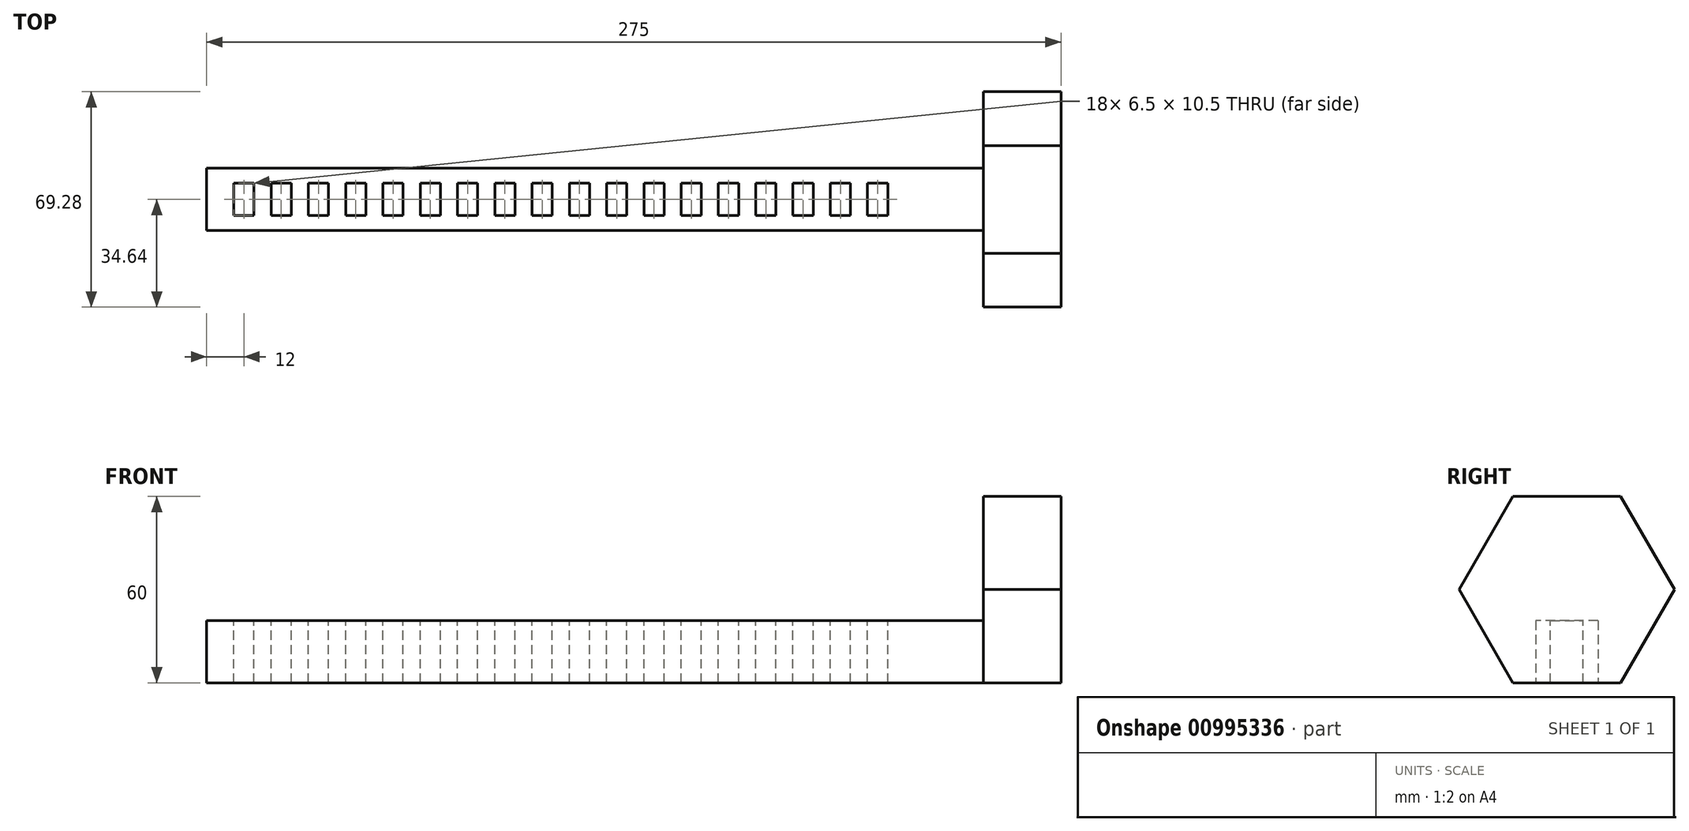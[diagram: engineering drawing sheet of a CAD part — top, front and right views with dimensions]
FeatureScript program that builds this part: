
annotation { "Feature Type Name" : "Feature", "Feature Type Description" : "" }
export const myFeature = defineFeature(function(context is Context, id is Id, definition is map)
    precondition{}
    {
        {
            var Q0;
            Q0=qCreatedBy(makeId("Right.planeOp"),FACE);
            var sketch = newSketch(context, id + "F0", { "sketchPlane" : qUnion([Q0])});
            skPoint(sketch, "E0", {"position": v(0, 0) * mm});
            skPoint(sketch, "E1", {"position": v(0, 30) * mm});
            skCircle(sketch, "E2.cCircle", {"center": v(0, 30) * mm, "radius": 30 * mm, "construction": true});
            skLineSegment(sketch, "E2.0", {"start": v(17.32, 0) * mm, "end": v(-17.32, 0) * mm});
            skLineSegment(sketch, "E2.1", {"start": v(-17.32, 0) * mm, "end": v(-34.64, 30) * mm});
            skLineSegment(sketch, "E2.2", {"start": v(-34.64, 30) * mm, "end": v(-17.32, 60) * mm});
            skLineSegment(sketch, "E2.3", {"start": v(-17.32, 60) * mm, "end": v(17.32, 60) * mm});
            skLineSegment(sketch, "E2.4", {"start": v(17.32, 60) * mm, "end": v(34.64, 30) * mm});
            skLineSegment(sketch, "E2.5", {"start": v(34.64, 30) * mm, "end": v(17.32, 0) * mm});
            skSolve(sketch);
        }
        {
            var Q0;
            Q0 = qSketchRegion(id + "F0", true);
            extrude(context, id + "F1", {"entities" : qUnion([Q0]), "depth" : 25 * mm, "offsetDistance" : 25 * mm});
        }
        {
            var Q0;
            Q0=qCreatedBy(makeId("Top.planeOp"),FACE);
            var sketch = newSketch(context, id + "F2", { "sketchPlane" : qUnion([Q0])});
            skPoint(sketch, "E3", {"position": v(0, 0) * mm});
            skPoint(sketch, "E4", {"position": v(0, 10) * mm});
            skPoint(sketch, "E5", {"position": v(0, -10) * mm});
            skLineSegment(sketch, "E6.bottom", {"start": v(0, 10) * mm, "end": v(-250, 10) * mm});
            skLineSegment(sketch, "E6.top", {"start": v(0, -10) * mm, "end": v(-250, -10) * mm});
            skLineSegment(sketch, "E6.left", {"start": v(0, 10) * mm, "end": v(0, -10) * mm});
            skLineSegment(sketch, "E6.right", {"start": v(-250, 10) * mm, "end": v(-250, -10) * mm});
            skSolve(sketch);
        }
        {
            var Q0;
            Q0 = qSketchRegion(id + "F2", true);
            extrude(context, id + "F3", {"entities" : qUnion([Q0]), "operationType" : NewBodyOperationType.ADD, "depth" : 20 * mm, "offsetDistance" : 25 * mm});
        }
        {
            var Q0;
            Q0=makeQuery(id+"F3.opExtrude","CAP_FACE",FACE,{"disambiguationData":[OSD([sQuery(id+"F2.wireOp",EDGE,"E6.bottom"),sQuery(id+"F2.wireOp",EDGE,"E6.top"),sQuery(id+"F2.wireOp",EDGE,"E6.left"),sQuery(id+"F2.wireOp",EDGE,"E6.right")])],"isStart":false});
            var sketch = newSketch(context, id + "F4", { "sketchPlane" : qUnion([Q0])});
            skPoint(sketch, "E7", {"position": v(-10, 0) * mm});
            skPoint(sketch, "E8", {"position": v(0, 0) * mm});
            skLineSegment(sketch, "E9.bottom", {"start": v(-13.25, 5.25) * mm, "end": v(-6.75, 5.25) * mm});
            skLineSegment(sketch, "E9.top", {"start": v(-13.25, -5.25) * mm, "end": v(-6.75, -5.25) * mm});
            skLineSegment(sketch, "E9.left", {"start": v(-13.25, 5.25) * mm, "end": v(-13.25, -5.25) * mm});
            skLineSegment(sketch, "E9.right", {"start": v(-6.75, 5.25) * mm, "end": v(-6.75, -5.25) * mm});
            skPoint(sketch, "E10", {"position": v(-22, 0) * mm});
            skPoint(sketch, "E11", {"position": v(-34, 0) * mm});
            skLineSegment(sketch, "E12.bottom", {"start": v(-25.25, -5.25) * mm, "end": v(-18.75, -5.25) * mm});
            skLineSegment(sketch, "E12.top", {"start": v(-25.25, 5.25) * mm, "end": v(-18.75, 5.25) * mm});
            skLineSegment(sketch, "E12.left", {"start": v(-25.25, -5.25) * mm, "end": v(-25.25, 5.25) * mm});
            skLineSegment(sketch, "E12.right", {"start": v(-18.75, -5.25) * mm, "end": v(-18.75, 5.25) * mm});
            skLineSegment(sketch, "E13.bottom", {"start": v(-37.25, -5.25) * mm, "end": v(-30.75, -5.25) * mm});
            skLineSegment(sketch, "E13.top", {"start": v(-37.25, 5.25) * mm, "end": v(-30.75, 5.25) * mm});
            skLineSegment(sketch, "E13.left", {"start": v(-37.25, -5.25) * mm, "end": v(-37.25, 5.25) * mm});
            skLineSegment(sketch, "E13.right", {"start": v(-30.75, -5.25) * mm, "end": v(-30.75, 5.25) * mm});
            skPoint(sketch, "E14", {"position": v(-46, 0) * mm});
            skPoint(sketch, "E15", {"position": v(-58, 0) * mm});
            skPoint(sketch, "E16", {"position": v(-70, 0) * mm});
            skPoint(sketch, "E17", {"position": v(-82, 0) * mm});
            skLineSegment(sketch, "E18.bottom", {"start": v(-49.25, 5.25) * mm, "end": v(-42.75, 5.25) * mm});
            skLineSegment(sketch, "E18.top", {"start": v(-49.25, -5.25) * mm, "end": v(-42.75, -5.25) * mm});
            skLineSegment(sketch, "E18.left", {"start": v(-49.25, 5.25) * mm, "end": v(-49.25, -5.25) * mm});
            skLineSegment(sketch, "E18.right", {"start": v(-42.75, 5.25) * mm, "end": v(-42.75, -5.25) * mm});
            skLineSegment(sketch, "E19.bottom", {"start": v(-61.25, -5.25) * mm, "end": v(-54.75, -5.25) * mm});
            skLineSegment(sketch, "E19.top", {"start": v(-61.25, 5.25) * mm, "end": v(-54.75, 5.25) * mm});
            skLineSegment(sketch, "E19.left", {"start": v(-61.25, -5.25) * mm, "end": v(-61.25, 5.25) * mm});
            skLineSegment(sketch, "E19.right", {"start": v(-54.75, -5.25) * mm, "end": v(-54.75, 5.25) * mm});
            skLineSegment(sketch, "E20.bottom", {"start": v(-73.25, -5.25) * mm, "end": v(-66.75, -5.25) * mm});
            skLineSegment(sketch, "E20.top", {"start": v(-73.25, 5.25) * mm, "end": v(-66.75, 5.25) * mm});
            skLineSegment(sketch, "E20.left", {"start": v(-73.25, -5.25) * mm, "end": v(-73.25, 5.25) * mm});
            skLineSegment(sketch, "E20.right", {"start": v(-66.75, -5.25) * mm, "end": v(-66.75, 5.25) * mm});
            skLineSegment(sketch, "E21.bottom", {"start": v(-85.25, -5.25) * mm, "end": v(-78.75, -5.25) * mm});
            skLineSegment(sketch, "E21.top", {"start": v(-85.25, 5.25) * mm, "end": v(-78.75, 5.25) * mm});
            skLineSegment(sketch, "E21.left", {"start": v(-85.25, -5.25) * mm, "end": v(-85.25, 5.25) * mm});
            skLineSegment(sketch, "E21.right", {"start": v(-78.75, -5.25) * mm, "end": v(-78.75, 5.25) * mm});
            skPoint(sketch, "E22", {"position": v(-94, 0) * mm});
            skPoint(sketch, "E23", {"position": v(-106, 0) * mm});
            skPoint(sketch, "E24", {"position": v(-118, 0) * mm});
            skLineSegment(sketch, "E25.bottom", {"start": v(-97.25, -5.25) * mm, "end": v(-90.75, -5.25) * mm});
            skLineSegment(sketch, "E25.top", {"start": v(-97.25, 5.25) * mm, "end": v(-90.75, 5.25) * mm});
            skLineSegment(sketch, "E25.left", {"start": v(-97.25, -5.25) * mm, "end": v(-97.25, 5.25) * mm});
            skLineSegment(sketch, "E25.right", {"start": v(-90.75, -5.25) * mm, "end": v(-90.75, 5.25) * mm});
            skLineSegment(sketch, "E26.bottom", {"start": v(-109.25, -5.25) * mm, "end": v(-102.75, -5.25) * mm});
            skLineSegment(sketch, "E26.top", {"start": v(-109.25, 5.25) * mm, "end": v(-102.75, 5.25) * mm});
            skLineSegment(sketch, "E26.left", {"start": v(-109.25, -5.25) * mm, "end": v(-109.25, 5.25) * mm});
            skLineSegment(sketch, "E26.right", {"start": v(-102.75, -5.25) * mm, "end": v(-102.75, 5.25) * mm});
            skLineSegment(sketch, "E27.bottom", {"start": v(-114.75, -5.25) * mm, "end": v(-121.25, -5.25) * mm});
            skLineSegment(sketch, "E27.top", {"start": v(-114.75, 5.25) * mm, "end": v(-121.25, 5.25) * mm});
            skLineSegment(sketch, "E27.left", {"start": v(-114.75, -5.25) * mm, "end": v(-114.75, 5.25) * mm});
            skLineSegment(sketch, "E27.right", {"start": v(-121.25, -5.25) * mm, "end": v(-121.25, 5.25) * mm});
            skPoint(sketch, "E28", {"position": v(-124, 0) * mm});
            skPoint(sketch, "E29.startSnap0", {"position": v(-125, 10) * mm});
            skPoint(sketch, "E30.MirrorP", {"position": v(-130, 0) * mm});
            skLineSegment(sketch, "E31.MirrorCS", {"start": v(-133.25, -5.25) * mm, "end": v(-133.25, 5.25) * mm});
            skLineSegment(sketch, "E32.MirrorCS", {"start": v(-133.25, 5.25) * mm, "end": v(-126.75, 5.25) * mm});
            skLineSegment(sketch, "E33.MirrorCS", {"start": v(-126.75, -5.25) * mm, "end": v(-126.75, 5.25) * mm});
            skLineSegment(sketch, "E34.MirrorCS", {"start": v(-133.25, -5.25) * mm, "end": v(-126.75, -5.25) * mm});
            skLineSegment(sketch, "E35.MirrorCS", {"start": v(-138.75, -5.25) * mm, "end": v(-145.25, -5.25) * mm});
            skPoint(sketch, "E36.MirrorP", {"position": v(-142, 0) * mm});
            skLineSegment(sketch, "E37.MirrorCS", {"start": v(-138.75, -5.25) * mm, "end": v(-138.75, 5.25) * mm});
            skLineSegment(sketch, "E38.MirrorCS", {"start": v(-138.75, 5.25) * mm, "end": v(-145.25, 5.25) * mm});
            skLineSegment(sketch, "E39.MirrorCS", {"start": v(-145.25, -5.25) * mm, "end": v(-145.25, 5.25) * mm});
            skLineSegment(sketch, "E40.MirrorCS", {"start": v(-150.75, -5.25) * mm, "end": v(-150.75, 5.25) * mm});
            skLineSegment(sketch, "E41.MirrorCS", {"start": v(-157.25, -5.25) * mm, "end": v(-157.25, 5.25) * mm});
            skLineSegment(sketch, "E42.MirrorCS", {"start": v(-150.75, 5.25) * mm, "end": v(-157.25, 5.25) * mm});
            skLineSegment(sketch, "E43.MirrorCS", {"start": v(-150.75, -5.25) * mm, "end": v(-157.25, -5.25) * mm});
            skLineSegment(sketch, "E44.MirrorCS", {"start": v(-162.75, -5.25) * mm, "end": v(-169.25, -5.25) * mm});
            skLineSegment(sketch, "E45.MirrorCS", {"start": v(-162.75, -5.25) * mm, "end": v(-162.75, 5.25) * mm});
            skLineSegment(sketch, "E46.MirrorCS", {"start": v(-169.25, -5.25) * mm, "end": v(-169.25, 5.25) * mm});
            skLineSegment(sketch, "E47.MirrorCS", {"start": v(-162.75, 5.25) * mm, "end": v(-169.25, 5.25) * mm});
            skLineSegment(sketch, "E48.MirrorCS", {"start": v(-174.75, 5.25) * mm, "end": v(-181.25, 5.25) * mm});
            skLineSegment(sketch, "E49.MirrorCS", {"start": v(-174.75, -5.25) * mm, "end": v(-174.75, 5.25) * mm});
            skLineSegment(sketch, "E50.MirrorCS", {"start": v(-174.75, -5.25) * mm, "end": v(-181.25, -5.25) * mm});
            skLineSegment(sketch, "E51.MirrorCS", {"start": v(-181.25, -5.25) * mm, "end": v(-181.25, 5.25) * mm});
            skPoint(sketch, "E52.MirrorP", {"position": v(-190, 0) * mm});
            skLineSegment(sketch, "E53.MirrorCS", {"start": v(-186.75, -5.25) * mm, "end": v(-186.75, 5.25) * mm});
            skLineSegment(sketch, "E54.MirrorCS", {"start": v(-186.75, 5.25) * mm, "end": v(-193.25, 5.25) * mm});
            skLineSegment(sketch, "E55.MirrorCS", {"start": v(-193.25, -5.25) * mm, "end": v(-193.25, 5.25) * mm});
            skLineSegment(sketch, "E56.MirrorCS", {"start": v(-186.75, -5.25) * mm, "end": v(-193.25, -5.25) * mm});
            skLineSegment(sketch, "E57.MirrorCS", {"start": v(-198.75, 5.25) * mm, "end": v(-205.25, 5.25) * mm});
            skLineSegment(sketch, "E58.MirrorCS", {"start": v(-198.75, 5.25) * mm, "end": v(-198.75, -5.25) * mm});
            skLineSegment(sketch, "E59.MirrorCS", {"start": v(-205.25, 5.25) * mm, "end": v(-205.25, -5.25) * mm});
            skLineSegment(sketch, "E60.MirrorCS", {"start": v(-198.75, -5.25) * mm, "end": v(-205.25, -5.25) * mm});
            skPoint(sketch, "E61.MirrorP", {"position": v(-214, 0) * mm});
            skLineSegment(sketch, "E62.MirrorCS", {"start": v(-210.75, -5.25) * mm, "end": v(-210.75, 5.25) * mm});
            skLineSegment(sketch, "E63.MirrorCS", {"start": v(-210.75, -5.25) * mm, "end": v(-217.25, -5.25) * mm});
            skLineSegment(sketch, "E64.MirrorCS", {"start": v(-217.25, -5.25) * mm, "end": v(-217.25, 5.25) * mm});
            skLineSegment(sketch, "E65.MirrorCS", {"start": v(-210.75, 5.25) * mm, "end": v(-217.25, 5.25) * mm});
            skLineSegment(sketch, "E66.MirrorCS", {"start": v(-222.75, 5.25) * mm, "end": v(-229.25, 5.25) * mm});
            skLineSegment(sketch, "E67.MirrorCS", {"start": v(-222.75, -5.25) * mm, "end": v(-222.75, 5.25) * mm});
            skLineSegment(sketch, "E68.MirrorCS", {"start": v(-222.75, -5.25) * mm, "end": v(-229.25, -5.25) * mm});
            skLineSegment(sketch, "E69.MirrorCS", {"start": v(-229.25, -5.25) * mm, "end": v(-229.25, 5.25) * mm});
            skLineSegment(sketch, "E70.MirrorCS", {"start": v(-234.75, 5.25) * mm, "end": v(-241.25, 5.25) * mm});
            skLineSegment(sketch, "E71.MirrorCS", {"start": v(-234.75, 5.25) * mm, "end": v(-234.75, -5.25) * mm});
            skLineSegment(sketch, "E72.MirrorCS", {"start": v(-234.75, -5.25) * mm, "end": v(-241.25, -5.25) * mm});
            skLineSegment(sketch, "E73.MirrorCS", {"start": v(-241.25, 5.25) * mm, "end": v(-241.25, -5.25) * mm});
            skPoint(sketch, "E29.start.orphan", {"position": v(-124, 10) * mm});
            skSolve(sketch);
        }
        {
            var Q0;
            Q0 = qSketchRegion(id + "F4", true);
            extrude(context, id + "F5", {"entities" : qUnion([Q0]), "operationType" : NewBodyOperationType.REMOVE, "oppositeDirection" : true, "depth" : 100 * mm, "offsetDistance" : 25 * mm});
        }
        {
            var Q0;
            Q0=qCreatedBy(makeId("Top.planeOp"),FACE);
            var sketch = newSketch(context, id + "F6", { "sketchPlane" : qUnion([Q0])});
            skLineSegment(sketch, "E74.bottom", {"start": v(0, 7.37) * mm, "end": v(-28.43, 7.37) * mm});
            skLineSegment(sketch, "E74.top", {"start": v(0, -7.05) * mm, "end": v(-28.43, -7.05) * mm});
            skLineSegment(sketch, "E74.left", {"start": v(0, 7.37) * mm, "end": v(0, -7.05) * mm});
            skLineSegment(sketch, "E74.right", {"start": v(-28.43, 7.37) * mm, "end": v(-28.43, -7.05) * mm});
            skSolve(sketch);
        }
        {
            var Q0;
            Q0 = qSketchRegion(id + "F6", true);
            extrude(context, id + "F7", {"entities" : qUnion([Q0]), "operationType" : NewBodyOperationType.ADD, "depth" : 20 * mm, "offsetDistance" : 25 * mm});
        }
    });
